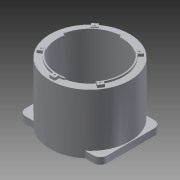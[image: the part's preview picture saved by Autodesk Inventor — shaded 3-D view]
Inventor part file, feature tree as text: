
AUTODESK INVENTOR PART (.ipt)
format: ipt  version: 2015 (Build 190159000, 159)  size: 388,096 bytes
history: native  units: mm
features: thread x9, sketch x7, extrude x7, other x3, hole x3, plane x1
ambient origin geometry x8: Origin, YZ Plane, XZ Plane, XY Plane, X Axis, Y Axis, Z Axis, Center Point
bodies: Solid1 (feature_tree)
feature tree (30):
  plane  "Work Plane2"
  sketch  "Sketch2"  dims[d0=-2.23mm d1=-1.9mm d2=58.0mm]
  sketch  "Sketch4"  dims[d6=47.0mm d7=33.8mm]
  other  "Focal plane"
  other  "Back origin"
  sketch  "Sketch3"  dims[d3=-46.5mm d5=16.9mm]
  sketch  "Sketch6"  dims[d10=3.5mm d11=2.0mm]
  sketch  "Sketch5"  dims[d8=25.2mm d9=22.8mm]
  extrude  "Extrusion2"  Depth=58.0mm
  extrude  "Extrusion16"  Depth=16.9mm
  extrude  "Extrusion4"  Depth=33.8mm
  extrude  "Extrusion5"  Depth=22.8mm
  sketch  "Sketch12"  dims[d12=4.0mm d13=4.0mm]
  extrude  "Extrusion10"  Depth=2.0mm
  extrude  "Extrusion13"  Depth=4.0mm
  extrude  "Extrusion15"  Depth=0.5mm
  hole  "Hole1"  [1 undecoded]
  thread  "Thread1"  [1 undecoded]
  thread  "Thread2"  [1 undecoded]
  thread  "Thread3"  [1 undecoded]
  thread  "Thread4"  [1 undecoded]
  thread  "Thread5"  [1 undecoded]
  hole  "Hole2"  [1 undecoded]
  thread  "Thread6"  [1 undecoded]
  thread  "Thread7"  [1 undecoded]
  hole  "Hole3"  [1 undecoded]
  thread  "Thread8"  [1 undecoded]
  thread  "Thread9"  [1 undecoded]
  other  "F-mount flange back plane"
  sketch  "Sketch15"  dims[d14=4.0mm d15=24.3mm d16=78.612601mm d17=73.221071mm d18=10.0mm d19=100.0mm d26=0.0mm d27=0.0mm d29=0.3mm d31=135.0deg d37=0.3mm d41=0.125mm d42=0.125mm d43=0.125mm d45=2.2125mm d47=0.5mm d52=-0.75mm d53=4.0mm d54=0.0mm d59=3.0mm d60=0.0mm d73=4.0mm d74=55.3mm d75=47.0mm d76=3.25mm d77=4.0mm d78=3.25mm d79=4.0mm d81=10.0mm d82=0.0mm d90=23.5mm d91=3.25mm d92=16.0mm d93=16.0mm d94=16.0mm d95=1.3mm d96=0.0mm d99=47.0mm d100=5.0mm d101=0.0mm d105=19.873663mm d106=13.803041mm d107=51.0mm d108=1.0mm d109=6.0mm d110=4.0mm d111=2.0mm d112=90.0deg d113=3.0mm d114=20.594885mm d115=10.0mm d116=0.0mm d117=10.0mm d118=0.0mm d119=10.0mm d120=0.0mm d121=10.0mm d122=0.0mm d123=10.0mm d124=0.0mm d135=59.3mm d136=44.3mm d137=5.0mm d138=4.0mm d139=0.0mm d140=0.75mm d141=0.0mm d142=1.95mm d143=6.0mm d144=4.0mm d145=2.0mm d146=90.0deg d147=8.0mm d148=20.594885mm d149=10.0mm d150=0.0mm d151=10.0mm d152=0.0mm d153=1.0mm d154=6.0mm d155=4.0mm d156=2.0mm d157=90.0deg d158=5.0mm d159=20.594885mm d160=10.0mm d161=0.0mm d162=10.0mm d163=0.0mm d164=55.0mm d165=25.0mm d166=2.0mm d167=0.0mm d168=25.0mm d169=34.7mm d170=0.0mm d171=0.0mm d172=6.15mm d173=6.2mm d186=1.0mm d187=1.0mm d189=1.0mm d190=27.8mm d191=28.7mm d192=27.8mm d193=14.35mm d194=13.9mm d195=0.5mm d196=0.5mm d197=0.5mm d198=0.5mm d199=0.5mm]
note: 12 required parameter values undecoded (feature->parameter linkage not recoverable at this tier; creation-order binding heuristic only, values carry confidence <= 0.55)
